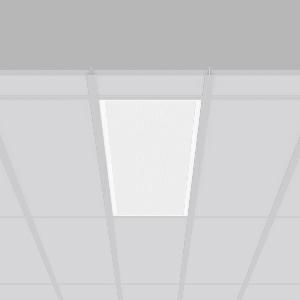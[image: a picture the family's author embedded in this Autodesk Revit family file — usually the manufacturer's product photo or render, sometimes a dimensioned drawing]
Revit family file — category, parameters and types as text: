
# Revit family: sidelite_eco_312366_002_1_76_42e7
name_source: partatom
category: Lighting Fixtures
units: mm (PartAtom-declared; Revit-internal decimal feet)

## family parameters
Cut with Voids When Loaded = No
Host = Face
Light Source = No
Part Type = Normal
Room Calculation Point = No
Round Connector Dimension = Use Diameter
Shared = No

## types (1)
- MultiLumen 1 (1 x LED Modul 840, 3500 lm, 4000)
    Apparent Load = 29 VA
    Approval mark = CE
    CIE Flux Codes = 63 88 97 100 100
    Color Rendering = 80
    Color Temperature = 4000
    Default Elevation = 1800 mm
    Description = Series: SIDELITE ECO
Highly economical recessed luminaire with progressive LED technology. Frame made of aluminium, powder-coated. Diffuser plastic microprismatic. Lightguide and diffuser made of non-yellowing plastic (PMMA). Lateral light emission (RZB SIDELITE technology) for homogeneous light distribution. External driver. External driver with simple plug-in locking system and extended converter connecting cable to luminaire (1.90 m). MultiLumen: 4 steps adjustable luminous flux. Factory setting is the lowest offered step. Luminaire can be used with accessories (to be ordered separately) for recessed, surface mounting or as pendant luminaire. Perfect for office areas (RUG < 19) and environments with computer screens in accordance with EN 12464-1. Qualified for use in the food and drink industry. 
Colour: white
Length: 1195 mm
Width: 295 mm
Cut-out length: 1180 mm
Cut-out width: 280 mm
Recess height: 160 mm
Luminaire: recess height: 38 mm
Lamp: LED
Socket: without socket
Colour temperature: 4000K
Colour rendering index (CRI): 80
System power: 29 W
Rated luminous flux: 3500 lm
Beam angle Down: 88° / 85°
Luminous efficiency: 121 lm/W
System power 2: 33 W
Rated luminous flux 2: 3850 lm
Luminous efficiency 2: 117 lm/W
System power 3: 35 W
Rated luminous flux 3: 4050 lm
Luminous efficiency 3: 116 lm/W
System power 4: 38 W
Rated luminous flux 4: 4400 lm
Luminous efficiency 4: 116 lm/W
Control gear: Converter, dimmable, DALI
Protection class: II
Type of protection: IP 40
    Height = 0 mm  [stored 0 ft]
    Lamp = 1 x LED Modul 840
    Lamp Light Flux = 3500 lm
    Lamp count = 1
    Length = 1195 mm
    Lifetime = 50000 h
    Luminous efficacy = 121 lm/W
    Manufacturer = RZB
    ModVariant = No
    Model = 312366.002.1.76
    Mounting Place = Ceiling
    Mounting Type = Recessed
    Number of Poles = 1
    OnlyDefault = Yes
    Power Factor = 1
    Product Name = SIDELITE ECO
    Product group = Recessed modular luminaires
    ProductGroupID = 406
    Protection Class = Protection class II
    Protection Degree = IP 40
    RLX_Detail_Level = 1
    RLX_Emergency_Light_Flux = 0 lm
    RLX_Emergency_Type = 0
    RLX_Emergency_Type_DB = No
    RlxData = <blob elided: 35973 chars, md5=d84beac5>
    Socket = socket
    Standby Power = 0 W
    System Light Flux = 3500 lm
    System Power = 29 W
    Type Comments = MultiLumen 1
    Type Image = 312366.002.jpg
    URL = http://relux.com
    VarID = multilumen_1
    Voltage = 230 V
    Voltage Range = 220-240 V
    Weight = 0.00 kg
    Width = 295 mm

note: [stored X ft] marks values corroborated as IEEE doubles in the binary element streams (Revit-internal decimal feet)

## geometry (parser evidence)
native form markers: Blend x4, Sweep x11
no freeform markers — native parametric forms only
